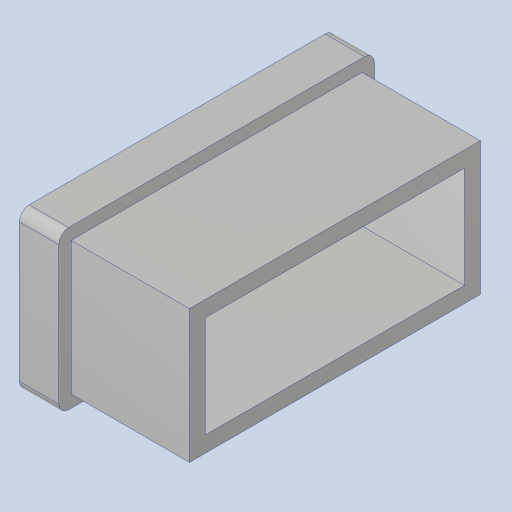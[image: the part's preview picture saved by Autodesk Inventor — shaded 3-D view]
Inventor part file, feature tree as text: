
AUTODESK INVENTOR PART (.ipt)
format: ipt  version: 2023.4 (Build 274418000, 418)  size: 292,864 bytes
history: native  units: in
note: dims shown in document units (in); Inventor stores cm internally (conversion verified against a paired STEP export)
features: sketch x3, extrude x2, shell x1, fillet x1, emboss x1
ambient origin geometry x8: Origin, YZ Plane, XZ Plane, XY Plane, X Axis, Y Axis, Z Axis, Center Point
bodies: Solid1 (feature_tree)
feature tree (8):
  extrude  "Extrusion1"  Depth=1.0in
  extrude  "Extrusion2"  Depth=0.0078in
  shell  "Shell1"  Thickness=0.25in
  fillet  "Fillet1"  Radius=0.0625in
  emboss  "Emboss1"
  sketch  "Sketch1"  dims[d0=2.0in d1=1.0in]
  sketch  "Sketch2"  dims[d4=0.0625in d5=0.0078in d6=0.25in d7=0.0in d8=0.0625in]
  sketch  "Sketch3"  dims[d9=0.0625in d10=0.0156in d11=0.75in d12=0.0in d13=0.1in d14=0.0625in d15=0.25in d16=0.0in]
